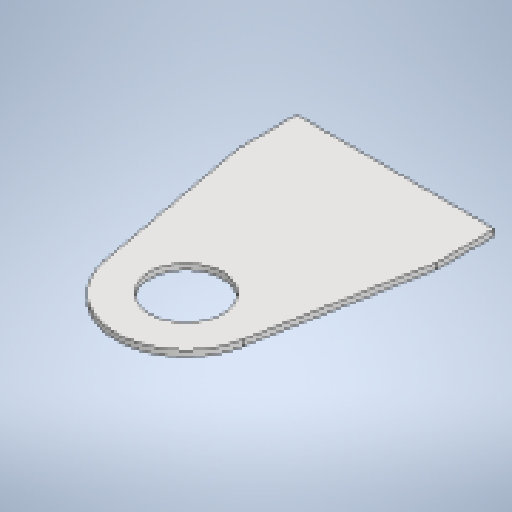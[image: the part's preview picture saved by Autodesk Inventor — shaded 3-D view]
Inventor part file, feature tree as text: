
AUTODESK INVENTOR PART (.ipt)
format: ipt  version: 2025.1 (Build 291241020, 241B)  size: 187,392 bytes
history: native  units: mm
features: sheet_metal_op x4, other x3, sketch x2
ambient origin geometry x8: Origin, YZ Plane, XZ Plane, XY Plane, X Axis, Y Axis, Z Axis, Center Point
bodies: Solid1 (feature_tree)
feature tree (9):
  sheet_metal_op  "Face1"
  sheet_metal_op  "Flange1"
  sketch  "Sketch1"  dims[d0=485.0mm]
  other  "Plate1"
  sketch  "Sketch2"  dims[d1=350.0mm d2=125.0mm d4=196.722284mm d5=10.0mm d6=10.0mm d7=5.0mm d8=20.0mm d9=10.0mm d10=40.0mm d11=60.0deg d12=1.0mm d13=40.0mm d14=10.0mm d15=10.0mm d16=5.759587mm d17=240.0mm]
  other  "Plate2"
  sheet_metal_op  "Bend1"
  sheet_metal_op  "Corner1"
  other  "Definition1"
